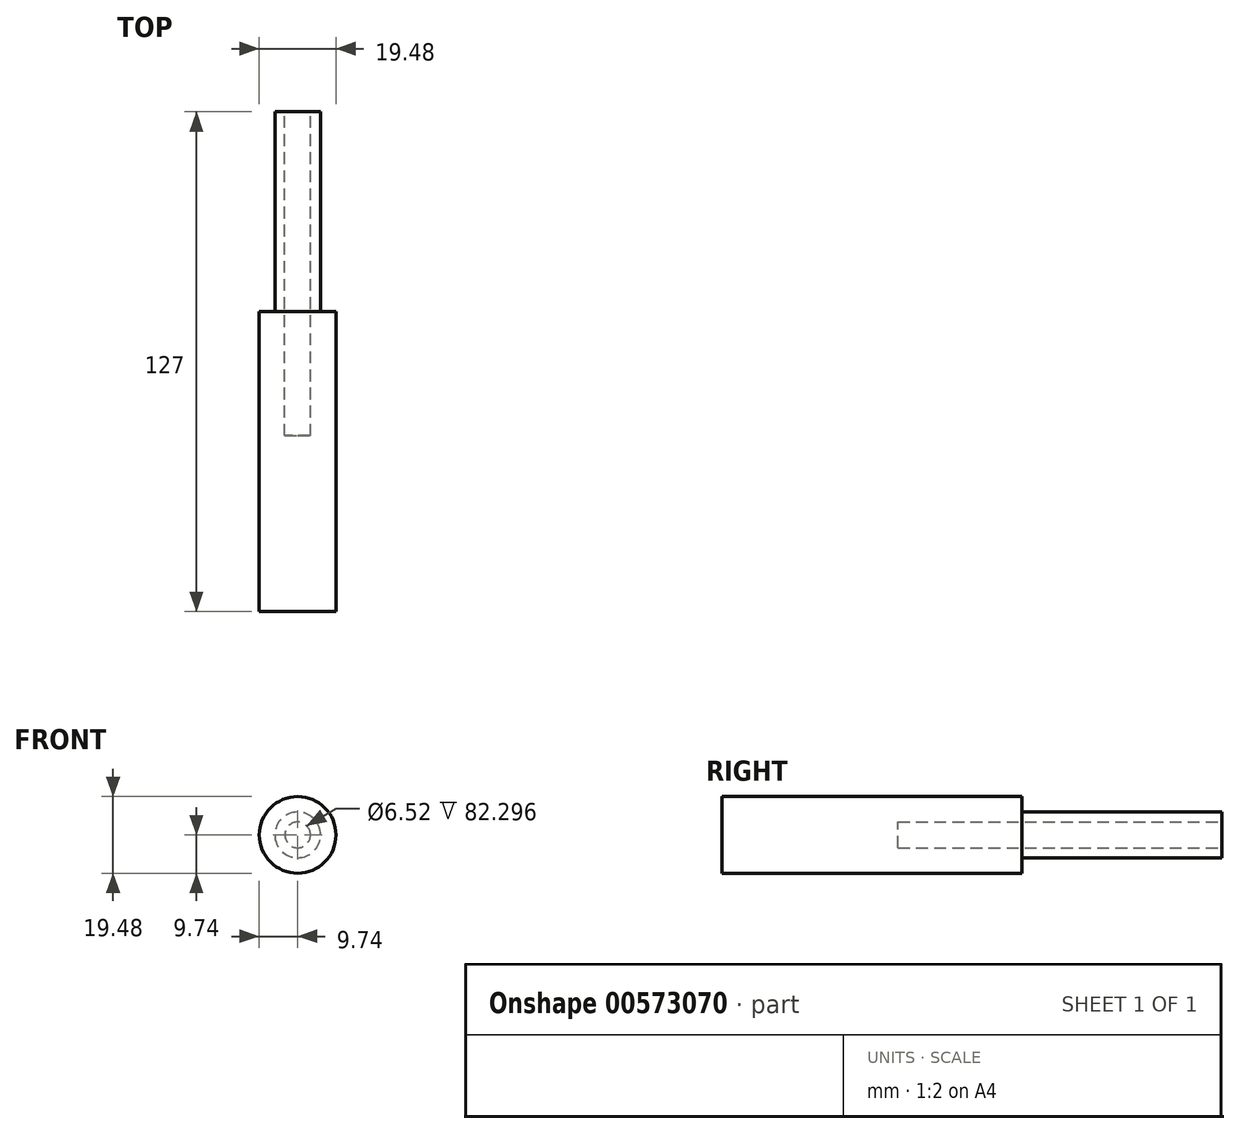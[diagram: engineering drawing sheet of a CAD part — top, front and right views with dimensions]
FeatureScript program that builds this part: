
annotation { "Feature Type Name" : "Feature", "Feature Type Description" : "" }
export const myFeature = defineFeature(function(context is Context, id is Id, definition is map)
    precondition{}
    {
        {
            var Q0;
            Q0=qCreatedBy(makeId("Top.planeOp"),FACE);
            var sketch = newSketch(context, id + "F0", { "sketchPlane" : qUnion([Q0])});
            skLineSegment(sketch, "E0.bottom", {"start": v(-5.34, 0) * mm, "end": v(5.8, 0) * mm});
            skLineSegment(sketch, "E0.top", {"start": v(-5.34, -50.8) * mm, "end": v(5.8, -50.8) * mm});
            skLineSegment(sketch, "E0.left", {"start": v(-5.34, 0) * mm, "end": v(-5.34, -50.8) * mm});
            skLineSegment(sketch, "E0.right", {"start": v(5.8, 0) * mm, "end": v(5.8, -50.8) * mm});
            skLineSegment(sketch, "E1.bottom", {"start": v(-8.58, -50.8) * mm, "end": v(9.74, -50.8) * mm});
            skLineSegment(sketch, "E1.top", {"start": v(-8.58, -127) * mm, "end": v(9.74, -127) * mm});
            skLineSegment(sketch, "E1.left", {"start": v(-8.58, -50.8) * mm, "end": v(-8.58, -127) * mm});
            skLineSegment(sketch, "E1.right", {"start": v(9.74, -50.8) * mm, "end": v(9.74, -127) * mm});
            skLineSegment(sketch, "E2", {"start": v(0, 0) * mm, "end": v(0, -127) * mm});
            skSolve(sketch);
        }
        {
            var Q0;
            {var subQ0=sQuery(id+"F0.wireOp",EDGE,"E0.right");Q0=makeQuery(id+"F0.imprint","IMPRINT",FACE,{"disambiguationData":[TD([[makeQuery(id+"F0.imprint","IMPRINT",EDGE,{"derivedFrom":subQ0}),-1.0]])]});}
            var Q1;
            {var subQ0=sQuery(id+"F0.wireOp",EDGE,"E1.right");Q1=makeQuery(id+"F0.imprint","IMPRINT",FACE,{"disambiguationData":[TD([[makeQuery(id+"F0.imprint","IMPRINT",EDGE,{"derivedFrom":subQ0}),-1.0]])]});}
            var Q2;
            Q2=sQuery(id+"F0.wireOp",EDGE,"E2");
            revolve(context, id + "F1", {"entities" : qUnion([Q0, Q1]), "axis" : qUnion([Q2]), "revolveType" : RevolveType.FULL});
        }
        {
            var Q0;
            Q0=qCreatedBy(makeId("Front.planeOp"),FACE);
            var sketch = newSketch(context, id + "F2", { "sketchPlane" : qUnion([Q0])});
            skCircle(sketch, "E3", {"center": v(0, 0) * mm, "radius": 3.26 * mm});
            skSolve(sketch);
        }
        {
            var Q0;
            Q0 = qSketchRegion(id + "F2", true);
            extrude(context, id + "F3", {"entities" : qUnion([Q0]), "depth" : 82.3 * mm, "offsetDistance" : 25.4 * mm});
        }
        {
            var Q0;
            Q0=makeQuery(id+"F3.opExtrude","SWEPT_BODY",BODY,{"disambiguationData":[OSD([sQuery(id+"F2.wireOp",EDGE,"E3")])]});
            var Q1;
            Q1=makeQuery(id+"F1.opRevolve","SWEPT_BODY",BODY,{"disambiguationData":[OSD([sQuery(id+"F0.wireOp",EDGE,"E0.bottom"),sQuery(id+"F0.wireOp",EDGE,"E0.right"),sQuery(id+"F0.wireOp",EDGE,"E1.bottom"),sQuery(id+"F0.wireOp",EDGE,"E1.top"),sQuery(id+"F0.wireOp",EDGE,"E1.right"),sQuery(id+"F0.wireOp",EDGE,"E2")])]});
            booleanBodies(context, id + "F4", {"operationType" : BooleanOperationType.SUBTRACTION, "tools" : qUnion([Q0]), "targets" : qUnion([Q1])});
        }
    });
